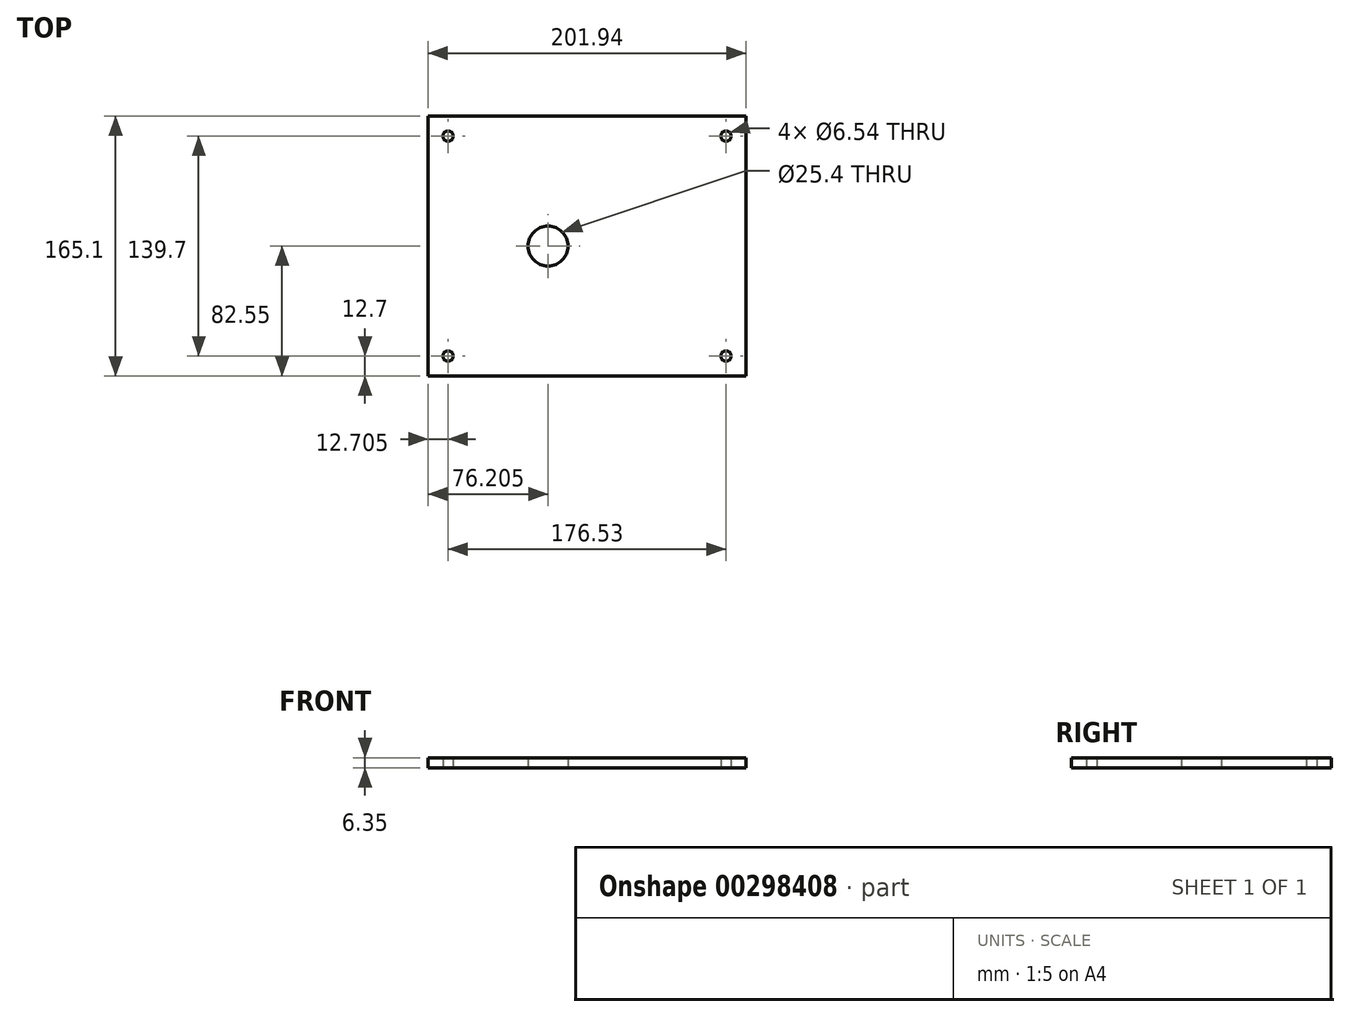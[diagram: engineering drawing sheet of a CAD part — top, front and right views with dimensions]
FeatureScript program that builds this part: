
annotation { "Feature Type Name" : "Feature", "Feature Type Description" : "" }
export const myFeature = defineFeature(function(context is Context, id is Id, definition is map)
    precondition{}
    {
        {
            var Q0;
            Q0=qCreatedBy(makeId("Top.planeOp"),FACE);
            var sketch = newSketch(context, id + "F0", { "sketchPlane" : qUnion([Q0])});
            skLineSegment(sketch, "E0.bottom", {"start": v(100.97, 82.55) * mm, "end": v(-100.97, 82.55) * mm});
            skLineSegment(sketch, "E0.top", {"start": v(100.97, -82.55) * mm, "end": v(-100.97, -82.55) * mm});
            skLineSegment(sketch, "E0.left", {"start": v(100.97, 82.55) * mm, "end": v(100.97, -82.55) * mm});
            skLineSegment(sketch, "E0.right", {"start": v(-100.97, 82.55) * mm, "end": v(-100.97, -82.55) * mm});
            skPoint(sketch, "E0.middle", {"position": v(0, 0) * mm});
            skCircle(sketch, "E1", {"center": v(-88.27, 69.85) * mm, "radius": 3.27 * mm});
            skCircle(sketch, "E2.0.1.0", {"center": v(-88.27, -69.85) * mm, "radius": 3.27 * mm});
            skCircle(sketch, "E2.1.0.0", {"center": v(88.26, 69.85) * mm, "radius": 3.27 * mm});
            skCircle(sketch, "E2.1.1.0", {"center": v(88.26, -69.85) * mm, "radius": 3.27 * mm});
            skLineSegment(sketch, "E2.direction1", {"start": v(-88.27, 69.85) * mm, "end": v(88.26, 69.85) * mm, "construction": true});
            skLineSegment(sketch, "E2.direction2", {"start": v(-88.27, 69.85) * mm, "end": v(-88.27, -69.85) * mm, "construction": true});
            skCircle(sketch, "E3", {"center": v(-24.77, 0) * mm, "radius": 12.7 * mm});
            skSolve(sketch);
        }
        {
            var Q0;
            Q0 = qSketchRegion(id + "F0", true);
            extrude(context, id + "F1", {"entities" : qUnion([Q0]), "depth" : 6.35 * mm});
        }
    });
